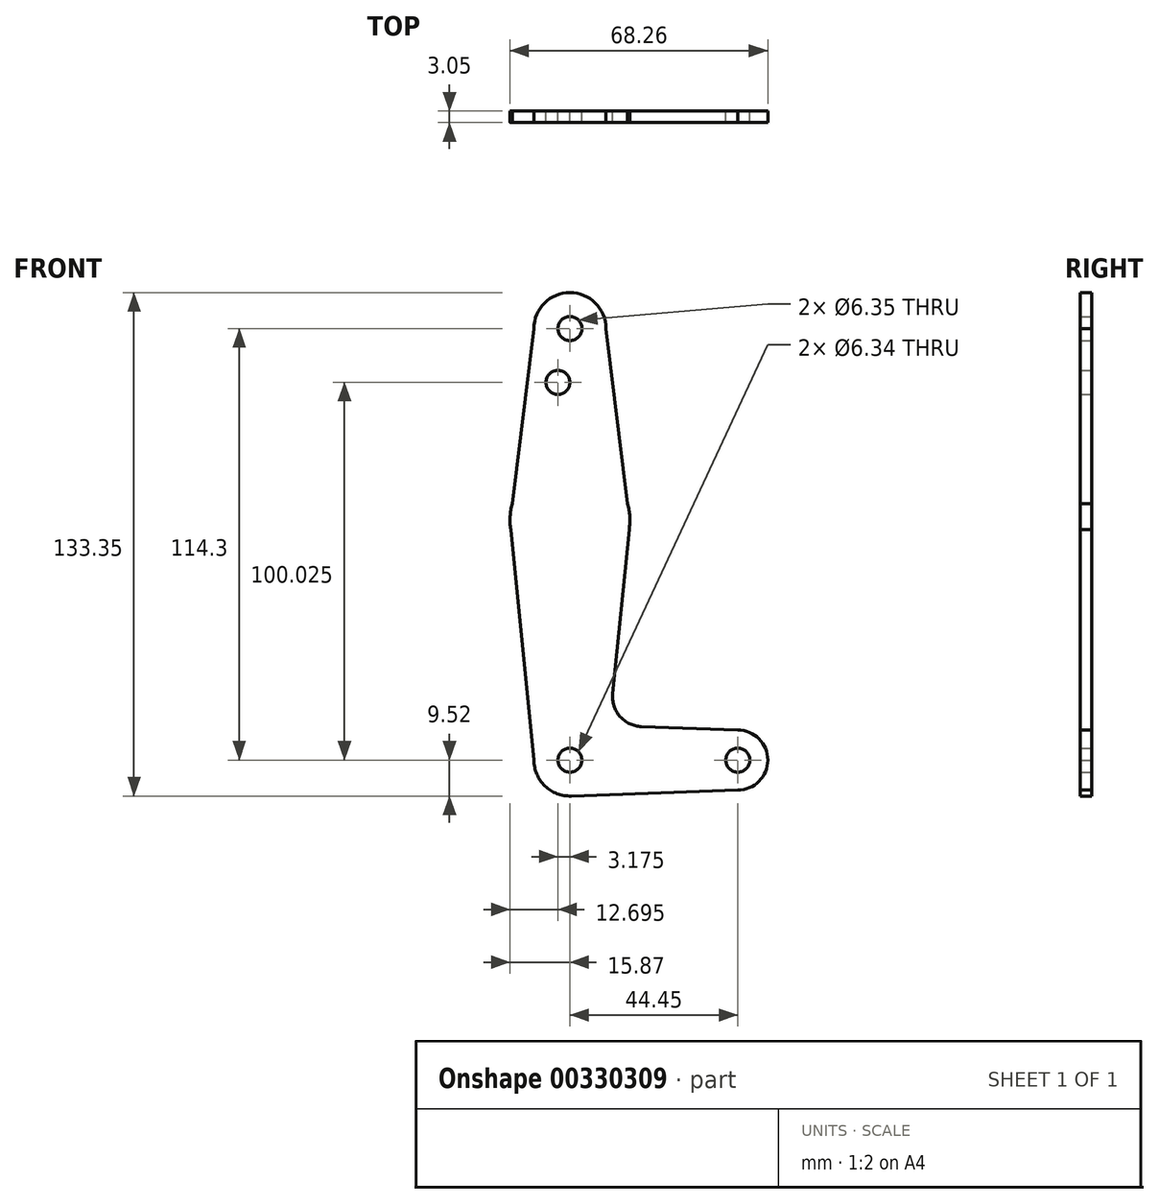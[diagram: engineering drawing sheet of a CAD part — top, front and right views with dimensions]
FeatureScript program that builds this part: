
annotation { "Feature Type Name" : "Feature", "Feature Type Description" : "" }
export const myFeature = defineFeature(function(context is Context, id is Id, definition is map)
    precondition{}
    {
        {
            var Q0;
            Q0=qCreatedBy(makeId("Front.planeOp"),FACE);
            var sketch = newSketch(context, id + "F0", { "sketchPlane" : qUnion([Q0])});
            skLineSegment(sketch, "E0", {"start": v(0, 0) * mm, "end": v(3.17, 0) * mm, "construction": true});
            skLineSegment(sketch, "E1", {"start": v(0, 0) * mm, "end": v(0, 3.17) * mm, "construction": true});
            skArc(sketch, "E2", {"start": v(9.53, 114.3) * mm, "mid": v(0, 123.83) * mm, "end": v(-9.53, 114.3) * mm});
            skArc(sketch, "E3", {"start": v(-9.52, 0) * mm, "mid": v(-6.61, -6.85) * mm, "end": v(0.34, -9.52) * mm});
            skArc(sketch, "E4", {"start": v(-15.26, 67.89) * mm, "mid": v(-15.84, 64.51) * mm, "end": v(-15.7, 61.08) * mm});
            skPoint(sketch, "E5.end.orphan", {"position": v(-20.46, 63.5) * mm});
            skPoint(sketch, "E5.start.orphan", {"position": v(-20.46, 0) * mm});
            skArc(sketch, "E6", {"start": v(44.45, -7.94) * mm, "mid": v(52.39, 0) * mm, "end": v(44.45, 7.94) * mm});
            skLineSegment(sketch, "E7", {"start": v(9.53, 114.3) * mm, "end": v(15.26, 67.89) * mm});
            skLineSegment(sketch, "E8", {"start": v(-9.53, 114.3) * mm, "end": v(-15.26, 67.89) * mm});
            skLineSegment(sketch, "E9", {"start": v(15.7, 61.08) * mm, "end": v(11.33, 17.58) * mm});
            skLineSegment(sketch, "E10", {"start": v(-9.52, 0) * mm, "end": v(-15.7, 61.08) * mm});
            skLineSegment(sketch, "E11", {"start": v(44.45, -7.94) * mm, "end": v(0, -9.53) * mm});
            skLineSegment(sketch, "E12", {"start": v(44.45, 7.94) * mm, "end": v(18.96, 8.85) * mm});
            skCircle(sketch, "E13", {"center": v(0, 114.3) * mm, "radius": 3.18 * mm});
            skCircle(sketch, "E14", {"center": v(0, 0) * mm, "radius": 3.17 * mm});
            skCircle(sketch, "E15", {"center": v(44.45, 0) * mm, "radius": 3.18 * mm});
            skArc(sketch, "E16.filletArc", {"start": v(11.33, 17.58) * mm, "mid": v(13.25, 11.56) * mm, "end": v(18.96, 8.85) * mm});
            skLineSegment(sketch, "E17", {"start": v(0, 100.03) * mm, "end": v(0, 100.03) * mm});
            skCircle(sketch, "E18", {"center": v(-3.18, 100.03) * mm, "radius": 3.17 * mm});
            skPoint(sketch, "E19.end.orphan", {"position": v(30.28, 100.03) * mm});
            skPoint(sketch, "E19.start.orphan", {"position": v(30.28, 63.5) * mm});
            skArc(sketch, "E20.trimOffspring", {"start": v(15.7, 61.08) * mm, "mid": v(15.84, 64.51) * mm, "end": v(15.26, 67.89) * mm});
            skSolve(sketch);
        }
        {
            var Q0;
            Q0 = qSketchRegion(id + "F0", true);
            extrude(context, id + "F1", {"entities" : qUnion([Q0]), "depth" : 3.05 * mm});
        }
    });
